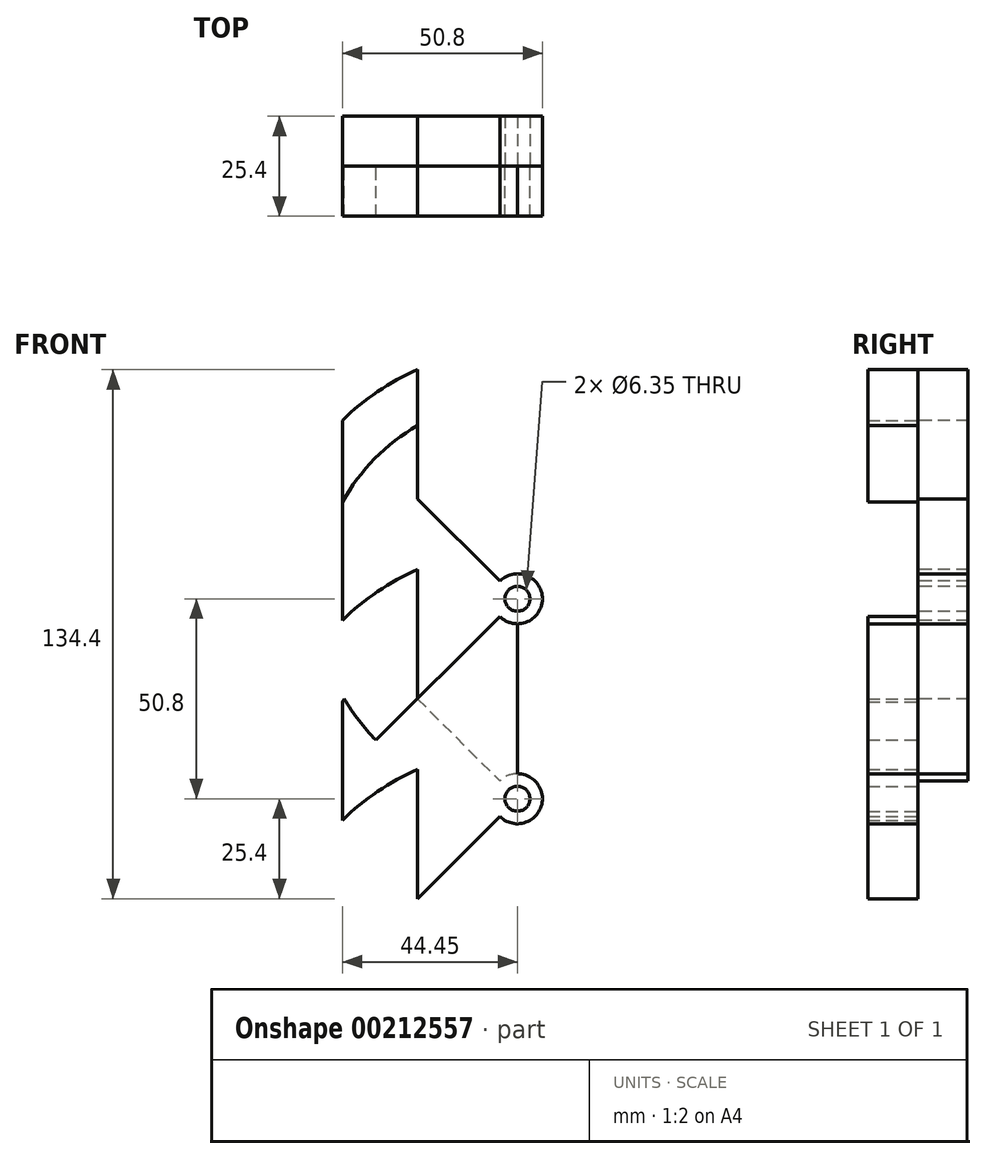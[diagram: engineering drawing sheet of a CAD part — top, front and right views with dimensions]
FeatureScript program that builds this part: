
annotation { "Feature Type Name" : "Feature", "Feature Type Description" : "" }
export const myFeature = defineFeature(function(context is Context, id is Id, definition is map)
    precondition{}
    {
        {
            var Q0;
            Q0=qCreatedBy(makeId("Front.planeOp"),FACE);
            var sketch = newSketch(context, id + "F0", { "sketchPlane" : qUnion([Q0])});
            skCircle(sketch, "E0", {"center": v(0, 0) * mm, "radius": 6.35 * mm});
            skLineSegment(sketch, "E1", {"start": v(0, 0) * mm, "end": v(0, 50.8) * mm});
            skCircle(sketch, "E2", {"center": v(0, 50.8) * mm, "radius": 6.35 * mm});
            skLineSegment(sketch, "E3", {"start": v(0, 50.8) * mm, "end": v(-44.45, 6.35) * mm});
            skLineSegment(sketch, "E4", {"start": v(-44.45, 44.45) * mm, "end": v(0, 0) * mm});
            skLineSegment(sketch, "E5", {"start": v(-25.4, 25.4) * mm, "end": v(-25.4, -25.4) * mm});
            skLineSegment(sketch, "E6", {"start": v(-25.4, -25.4) * mm, "end": v(0, 0) * mm});
            skLineSegment(sketch, "E7", {"start": v(0, 0) * mm, "end": v(0, -50.8) * mm});
            skCircle(sketch, "E8", {"center": v(0, -50.8) * mm, "radius": 2.64 * mm});
            skLineSegment(sketch, "E9", {"start": v(0, 50.8) * mm, "end": v(-35.92, 86.72) * mm});
            skLineSegment(sketch, "E10", {"start": v(-25.4, 109) * mm, "end": v(-25.4, 25.4) * mm});
            skArc(sketch, "E11", {"start": v(-44.45, -26.2) * mm, "mid": v(-36.25, -15.2) * mm, "end": v(-25.4, -6.8) * mm});
            skLineSegment(sketch, "E12", {"start": v(-25.4, -25.4) * mm, "end": v(-44.45, -44.45) * mm});
            skArc(sketch, "E13", {"start": v(-25.4, 7.4) * mm, "mid": v(-35.51, 1.84) * mm, "end": v(-44.45, -5.45) * mm});
            skLineSegment(sketch, "E14", {"start": v(-44.45, -44.45) * mm, "end": v(-44.45, -26.2) * mm});
            skArc(sketch, "E15.0.1.0", {"start": v(-25.4, 109) * mm, "mid": v(-35.51, 103.44) * mm, "end": v(-44.45, 96.15) * mm});
            skArc(sketch, "E15.0.1.1", {"start": v(-44.45, 75.4) * mm, "mid": v(-36.25, 86.4) * mm, "end": v(-25.4, 94.8) * mm});
            skLineSegment(sketch, "E15.0.1.2", {"start": v(-44.45, -5.45) * mm, "end": v(-44.45, 96.15) * mm});
            skLineSegment(sketch, "E15.direction1", {"start": v(0, -50.8) * mm, "end": v(25.4, -50.8) * mm, "construction": true});
            skLineSegment(sketch, "E15.direction2", {"start": v(0, -50.8) * mm, "end": v(0, 50.8) * mm, "construction": true});
            skPoint(sketch, "E16.orphan", {"position": v(-44.45, 57.15) * mm});
            skCircle(sketch, "E17", {"center": v(0, 50.8) * mm, "radius": 3.18 * mm});
            skCircle(sketch, "E18", {"center": v(0, 0) * mm, "radius": 3.18 * mm});
            skArc(sketch, "E19.0.1.0", {"start": v(-25.4, 58.2) * mm, "mid": v(-35.51, 52.64) * mm, "end": v(-44.45, 45.35) * mm});
            skLineSegment(sketch, "E19.direction1", {"start": v(0, 50.8) * mm, "end": v(25.4, 50.8) * mm, "construction": true});
            skLineSegment(sketch, "E19.direction2", {"start": v(0, 50.8) * mm, "end": v(0, 0) * mm, "construction": true});
            skArc(sketch, "E20", {"start": v(-35.92, -35.92) * mm, "mid": v(-40.58, -30.56) * mm, "end": v(-44.45, -24.6) * mm});
            skArc(sketch, "E21.0.1.0", {"start": v(-35.92, 14.88) * mm, "mid": v(-40.58, 20.24) * mm, "end": v(-44.45, 26.2) * mm});
            skArc(sketch, "E21.0.1.1", {"start": v(-44.45, 24.6) * mm, "mid": v(-36.25, 35.6) * mm, "end": v(-25.4, 44) * mm});
            skLineSegment(sketch, "E21.direction1", {"start": v(-35.92, -35.92) * mm, "end": v(-10.52, -35.92) * mm, "construction": true});
            skLineSegment(sketch, "E21.direction2", {"start": v(-35.92, -35.92) * mm, "end": v(-35.92, 14.88) * mm, "construction": true});
            skSolve(sketch);
        }
        {
            var Q0;
            {var subQ1=sQuery(id+"F0.wireOp",EDGE,"E5");var subQ3=sQuery(id+"F0.wireOp",EDGE,"E11");var subQ4=makeQuery(id+"F0.imprint","INTERSECT",VERTEX,{"derivedFrom":[subQ1,subQ3]});Q0=makeQuery(id+"F0.imprint","IMPRINT",FACE,{"disambiguationData":[TD([[makeQuery(id+"F0.imprint","IMPRINT",EDGE,{"disambiguationData":[TD([[subQ4,1.0]])],"derivedFrom":subQ3}),-1.0]])]});}
            var Q1;
            {var subQ5=sQuery(id+"F0.wireOp",EDGE,"E0");var subQ7=sQuery(id+"F0.wireOp",EDGE,"E6");var subQ8=makeQuery(id+"F0.imprint","INTERSECT",VERTEX,{"derivedFrom":[subQ5,subQ7]});Q1=makeQuery(id+"F0.imprint","IMPRINT",FACE,{"disambiguationData":[TD([[makeQuery(id+"F0.imprint","IMPRINT",EDGE,{"disambiguationData":[TD([[subQ8,1.0]])],"derivedFrom":subQ5}),-1.0]])]});}
            var Q2;
            {var subQ5=sQuery(id+"F0.wireOp",EDGE,"E1");var subQ7=sQuery(id+"F0.wireOp",EDGE,"E0");var subQ8=makeQuery(id+"F0.imprint","INTERSECT",VERTEX,{"derivedFrom":[subQ7,subQ5]});Q2=makeQuery(id+"F0.imprint","IMPRINT",FACE,{"disambiguationData":[TD([[makeQuery(id+"F0.imprint","IMPRINT",EDGE,{"disambiguationData":[TD([[subQ8,-1.0]])],"derivedFrom":subQ7}),-1.0]])]});}
            var Q3;
            {var subQ3=sQuery(id+"F0.wireOp",EDGE,"E13");Q3=makeQuery(id+"F0.imprint","IMPRINT",FACE,{"disambiguationData":[TD([[makeQuery(id+"F0.imprint","IMPRINT",EDGE,{"derivedFrom":subQ3}),-1.0]])]});}
            var Q4;
            {var subQ0=sQuery(id+"F0.wireOp",EDGE,"E7");var subQ1=sQuery(id+"F0.wireOp",EDGE,"E0");var subQ2=makeQuery(id+"F0.imprint","INTERSECT",VERTEX,{"derivedFrom":[subQ1,subQ0]});Q4=makeQuery(id+"F0.imprint","IMPRINT",FACE,{"disambiguationData":[TD([[makeQuery(id+"F0.imprint","IMPRINT",EDGE,{"disambiguationData":[TD([[subQ2,-1.0]])],"derivedFrom":subQ1}),1.0]])]});}
            var Q5;
            {var subQ0=sQuery(id+"F0.wireOp",EDGE,"E6");var subQ1=sQuery(id+"F0.wireOp",EDGE,"E0");var subQ2=makeQuery(id+"F0.imprint","INTERSECT",VERTEX,{"derivedFrom":[subQ1,subQ0]});Q5=makeQuery(id+"F0.imprint","IMPRINT",FACE,{"disambiguationData":[TD([[makeQuery(id+"F0.imprint","IMPRINT",EDGE,{"disambiguationData":[TD([[subQ2,1.0]])],"derivedFrom":subQ1}),1.0]])]});}
            var Q6;
            {var subQ0=sQuery(id+"F0.wireOp",EDGE,"E1");var subQ1=sQuery(id+"F0.wireOp",EDGE,"E0");var subQ2=makeQuery(id+"F0.imprint","INTERSECT",VERTEX,{"derivedFrom":[subQ1,subQ0]});Q6=makeQuery(id+"F0.imprint","IMPRINT",FACE,{"disambiguationData":[TD([[makeQuery(id+"F0.imprint","IMPRINT",EDGE,{"disambiguationData":[TD([[subQ2,-1.0]])],"derivedFrom":subQ1}),1.0]])]});}
            var Q7;
            {var subQ0=sQuery(id+"F0.wireOp",EDGE,"E7");var subQ1=sQuery(id+"F0.wireOp",EDGE,"E0");var subQ2=makeQuery(id+"F0.imprint","INTERSECT",VERTEX,{"derivedFrom":[subQ1,subQ0]});Q7=makeQuery(id+"F0.imprint","IMPRINT",FACE,{"disambiguationData":[TD([[makeQuery(id+"F0.imprint","IMPRINT",EDGE,{"disambiguationData":[TD([[subQ2,1.0]])],"derivedFrom":subQ1}),1.0]])]});}
            var Q8;
            {var subQ6=sQuery(id+"F0.wireOp",EDGE,"E15.0.1.0");Q8=makeQuery(id+"F0.imprint","IMPRINT",FACE,{"disambiguationData":[TD([[makeQuery(id+"F0.imprint","IMPRINT",EDGE,{"derivedFrom":subQ6}),1.0]])]});}
            var Q9;
            {var subQ0=sQuery(id+"F0.wireOp",EDGE,"E15.0.1.2");var subQ1=sQuery(id+"F0.wireOp",EDGE,"E3");var subQ2=makeQuery(id+"F0.imprint","INTERSECT",VERTEX,{"derivedFrom":[subQ1,subQ0]});Q9=makeQuery(id+"F0.imprint","IMPRINT",FACE,{"disambiguationData":[TD([[makeQuery(id+"F0.imprint","IMPRINT",EDGE,{"disambiguationData":[TD([[subQ2,1.0]])],"derivedFrom":subQ1}),-1.0]])]});}
            extrude(context, id + "F1", {"entities" : qUnion([Q0, Q1, Q2, Q3, Q4, Q5, Q6, Q7, Q8, Q9]), "depth" : 12.7 * mm});
        }
        {
            var Q0;
            {var subQ2=sQuery(id+"F0.wireOp",EDGE,"E9");var subQ4=sQuery(id+"F0.wireOp",EDGE,"E2");var subQ5=makeQuery(id+"F0.imprint","INTERSECT",VERTEX,{"derivedFrom":[subQ4,subQ2]});Q0=makeQuery(id+"F0.imprint","IMPRINT",FACE,{"disambiguationData":[TD([[makeQuery(id+"F0.imprint","IMPRINT",EDGE,{"disambiguationData":[TD([[subQ5,-1.0]])],"derivedFrom":subQ4}),-1.0]])]});}
            var Q1;
            {var subQ3=sQuery(id+"F0.wireOp",EDGE,"E19.0.1.0");Q1=makeQuery(id+"F0.imprint","IMPRINT",FACE,{"disambiguationData":[TD([[makeQuery(id+"F0.imprint","IMPRINT",EDGE,{"derivedFrom":subQ3}),-1.0]])]});}
            var Q2;
            {var subQ0=sQuery(id+"F0.wireOp",EDGE,"E15.0.1.1");var subQ1=sQuery(id+"F0.wireOp",EDGE,"E9");var subQ2=makeQuery(id+"F0.imprint","INTERSECT",VERTEX,{"derivedFrom":[subQ1,subQ0]});Q2=makeQuery(id+"F0.imprint","IMPRINT",FACE,{"disambiguationData":[TD([[makeQuery(id+"F0.imprint","IMPRINT",EDGE,{"disambiguationData":[TD([[subQ2,1.0]])],"derivedFrom":subQ1}),-1.0]])]});}
            var Q3;
            {var subQ6=sQuery(id+"F0.wireOp",EDGE,"E15.0.1.0");Q3=makeQuery(id+"F0.imprint","IMPRINT",FACE,{"disambiguationData":[TD([[makeQuery(id+"F0.imprint","IMPRINT",EDGE,{"derivedFrom":subQ6}),1.0]])]});}
            var Q4;
            {var subQ0=sQuery(id+"F0.wireOp",EDGE,"E9");var subQ1=sQuery(id+"F0.wireOp",EDGE,"E2");var subQ2=makeQuery(id+"F0.imprint","INTERSECT",VERTEX,{"derivedFrom":[subQ1,subQ0]});Q4=makeQuery(id+"F0.imprint","IMPRINT",FACE,{"disambiguationData":[TD([[makeQuery(id+"F0.imprint","IMPRINT",EDGE,{"disambiguationData":[TD([[subQ2,-1.0]])],"derivedFrom":subQ1}),1.0]])]});}
            var Q5;
            {var subQ0=sQuery(id+"F0.wireOp",EDGE,"E2");var subQ1=sQuery(id+"F0.wireOp",EDGE,"E1");var subQ2=makeQuery(id+"F0.imprint","INTERSECT",VERTEX,{"derivedFrom":[subQ1,subQ0]});Q5=makeQuery(id+"F0.imprint","IMPRINT",FACE,{"disambiguationData":[TD([[makeQuery(id+"F0.imprint","IMPRINT",EDGE,{"disambiguationData":[TD([[subQ2,-1.0]])],"derivedFrom":subQ1}),-1.0]])]});}
            var Q6;
            {var subQ0=sQuery(id+"F0.wireOp",EDGE,"E2");var subQ1=sQuery(id+"F0.wireOp",EDGE,"E1");var subQ2=makeQuery(id+"F0.imprint","INTERSECT",VERTEX,{"derivedFrom":[subQ1,subQ0]});Q6=makeQuery(id+"F0.imprint","IMPRINT",FACE,{"disambiguationData":[TD([[makeQuery(id+"F0.imprint","IMPRINT",EDGE,{"disambiguationData":[TD([[subQ2,-1.0]])],"derivedFrom":subQ1}),1.0]])]});}
            var Q7;
            {var subQ5=sQuery(id+"F0.wireOp",EDGE,"E1");var subQ7=sQuery(id+"F0.wireOp",EDGE,"E0");var subQ8=makeQuery(id+"F0.imprint","INTERSECT",VERTEX,{"derivedFrom":[subQ7,subQ5]});Q7=makeQuery(id+"F0.imprint","IMPRINT",FACE,{"disambiguationData":[TD([[makeQuery(id+"F0.imprint","IMPRINT",EDGE,{"disambiguationData":[TD([[subQ8,-1.0]])],"derivedFrom":subQ7}),-1.0]])]});}
            extrude(context, id + "F2", {"entities" : qUnion([Q0, Q1, Q2, Q3, Q4, Q5, Q6, Q7]), "oppositeDirection" : true, "depth" : 12.7 * mm});
        }
    });
